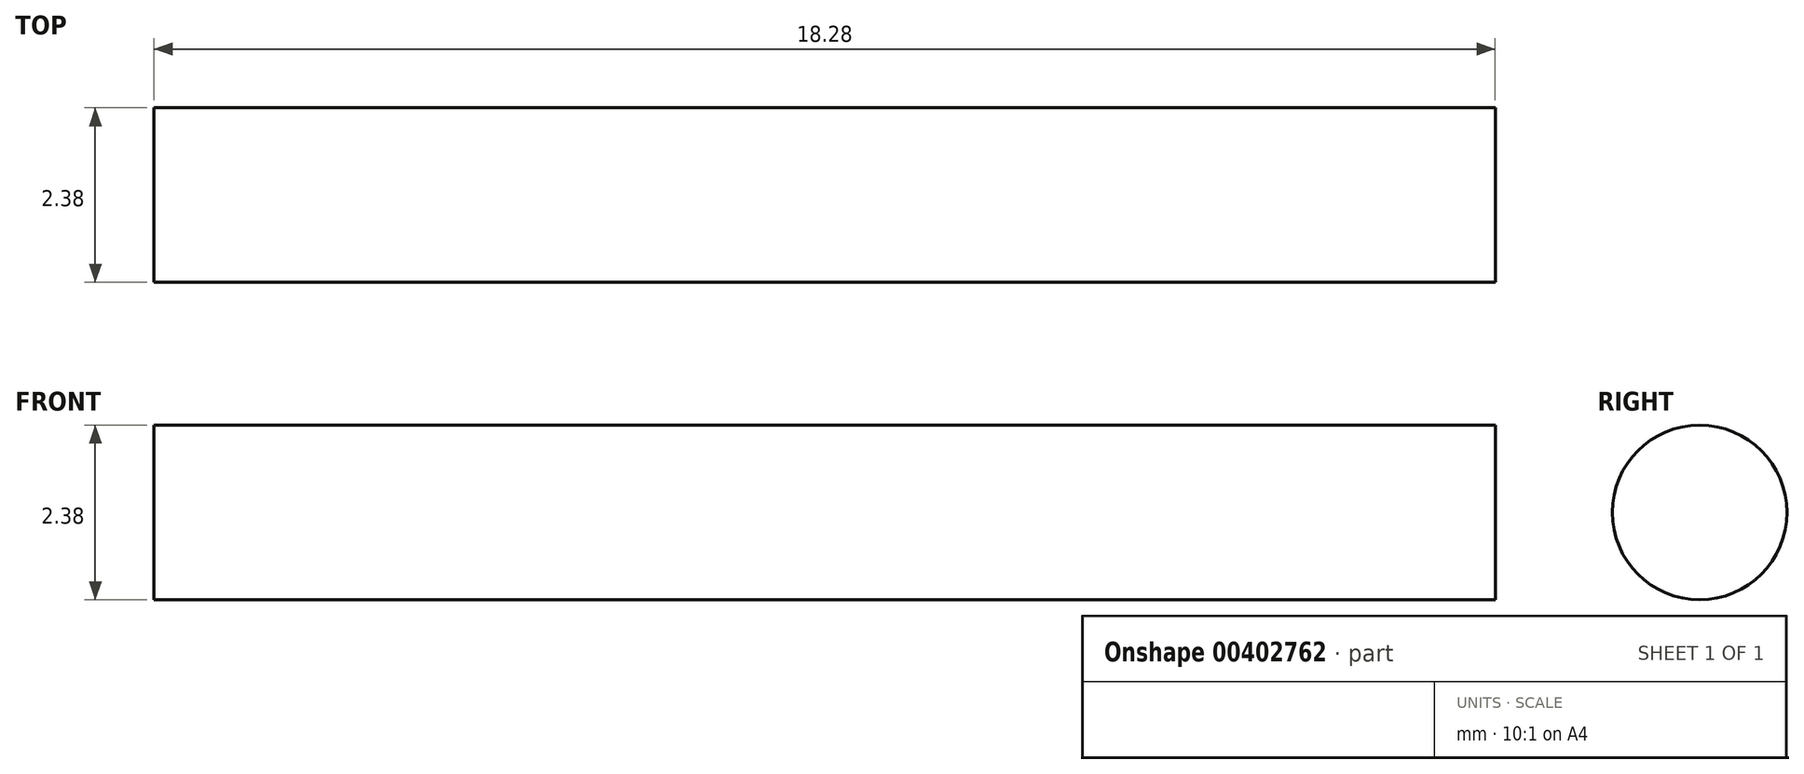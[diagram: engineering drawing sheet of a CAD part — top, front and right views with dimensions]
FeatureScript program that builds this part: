
annotation { "Feature Type Name" : "Feature", "Feature Type Description" : "" }
export const myFeature = defineFeature(function(context is Context, id is Id, definition is map)
    precondition{}
    {
        {
            var Q0;
            Q0=qCreatedBy(makeId("Right.planeOp"),FACE);
            var sketch = newSketch(context, id + "F0", { "sketchPlane" : qUnion([Q0])});
            skCircle(sketch, "E0", {"center": v(0, 0) * mm, "radius": 1.2 * mm});
            skSolve(sketch);
        }
        {
            var Q0;
            Q0=qSketchRegion(id+"F0",true);
            extrude(context, id + "F1", {"entities" : qUnion([Q0]), "endBound" : BoundingType.SYMMETRIC, "depth" : 18.29 * mm});
        }
    });
